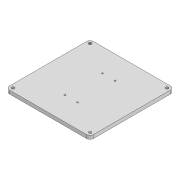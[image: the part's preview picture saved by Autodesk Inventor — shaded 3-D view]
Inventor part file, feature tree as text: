
AUTODESK INVENTOR PART (.ipt)
format: ipt  version: 2020 (Build 240168000, 168)  size: 125,952 bytes
history: native  units: mm
features: extrude x3, sketch x3, fillet x1
ambient origin geometry x8: Origin, YZ Plane, XZ Plane, XY Plane, X Axis, Y Axis, Z Axis, Center Point
bodies: Solid1 (feature_tree)
feature tree (7):
  extrude  "Extrusion1"  Depth=120.0mm
  extrude  "Extrusion2"  Depth=5.0mm
  fillet  "Fillet1"  Radius=110.0mm
  extrude  "Extrusion3"  Depth=10.0mm
  sketch  "Sketch1"  dims[d0=120.0mm d1=120.0mm]
  sketch  "Sketch2"  dims[d2=5.0mm d3=0.0mm d4=110.0mm d5=110.0mm]
  sketch  "Sketch3"  dims[d6=4.0mm d7=4.0mm d8=4.0mm d9=4.0mm d10=5.0mm d11=0.0mm d12=5.0mm d13=71.0mm d14=71.0mm d15=26.5mm d16=8.7mm d17=2.0mm d18=8.7mm d19=2.0mm d20=26.5mm d21=26.5mm d22=26.5mm d23=8.7mm d24=2.0mm d25=8.7mm d26=2.0mm d27=10.0mm d28=0.0mm]
